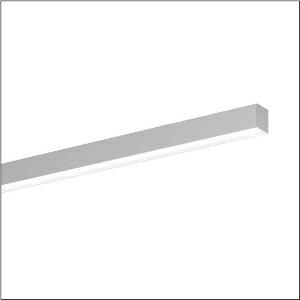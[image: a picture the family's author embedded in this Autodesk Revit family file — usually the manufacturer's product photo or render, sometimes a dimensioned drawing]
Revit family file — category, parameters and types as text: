
# Revit family: silica_r__21_51mx20dc35sb_d3c3
name_source: partatom
category: Lighting Fixtures
units: mm (PartAtom-declared; Revit-internal decimal feet)

## family parameters
Cut with Voids When Loaded = No
Host = Face
Light Source = No
Part Type = Normal
Room Calculation Point = No
Round Connector Dimension = Use Diameter
Shared = No

## types (1)
- --- (1 x LED, 6000 lm, 42.6 W, 3000K)
    Apparent Load = 43 VA
    CIE Flux Codes = 48 79 96 100 100
    Color Rendering = 80
    Color Temperature = 3000K
    Default Elevation = 1800 mm
    Description = Silica® 21, office luminaire, primary optical cover: cover, of PMMA, opal, light emission: direct distribution, primary light characteristic: symmetric, installation type: surface-mounted, LED, rated luminous flux: 6.000lm, luminous efficacy: 141lm/W, light colour: 830, colour temperature: 3000K, with terminal, 3+2-pole, max. 2.5mm², mains connection: 220..240V, AC, 50/60Hz, rated input power: 42.6W, luminaire housing, of aluminium, metallic grey (RAL 9006), length: 3.004mm, width: 53mm, height: 53mm, protection rating (complete): IP20, insulation class (complete): insulation class I (protective earthing), certification: CE, permissible operating ambient temperature: 0..+35°C, standard: EN 50419, packaging unit: 1 piece
    Height = 0 mm  [stored 0 ft]
    Lamp = 1 x LED
    Lamp Light Flux = 6000 lm
    Lamp Power = 42.6 W
    Lamp count = 1
    Length = 3004 mm
    Luminous efficacy = 141 lm/W
    Manufacturer = Siteco
    ModVariant = No
    Model = 51MX20DC35SB
    Mounting Place = Ceiling
    Mounting Type = Recessed
    Number of Poles = 1
    OnlyDefault = Yes
    Power Factor = 1
    Product Name = Silica® 21
    Product group = office luminaire | ceiling recessed
    ProductGroupID = 400
    Protection Class = Protection class I
    Protection Degree = IP 20
    RLX_Detail_Level = 1
    RLX_Emergency_Light_Flux = 0 lm
    RLX_Emergency_Type = 0
    RLX_Emergency_Type_DB = No
    RlxData = <blob elided: 26429 chars, md5=bd8aa456>
    Socket = socket
    Standby Power = 0 W
    System Light Flux = 6000 lm
    System Power = 43 W
    Type Comments = factory setting: luminous flux: 100 % | dim-lin: 254 | 233 mA
    Type Image = l_1335933.jpg
    URL = http://relux.com
    VarID = @adj_086645
    Voltage = 0 V
    Weight = 0.00 kg
    Width = 53 mm

note: [stored X ft] marks values corroborated as IEEE doubles in the binary element streams (Revit-internal decimal feet)

## geometry (parser evidence)
native form markers: Blend x4, Sweep x11
no freeform markers — native parametric forms only
